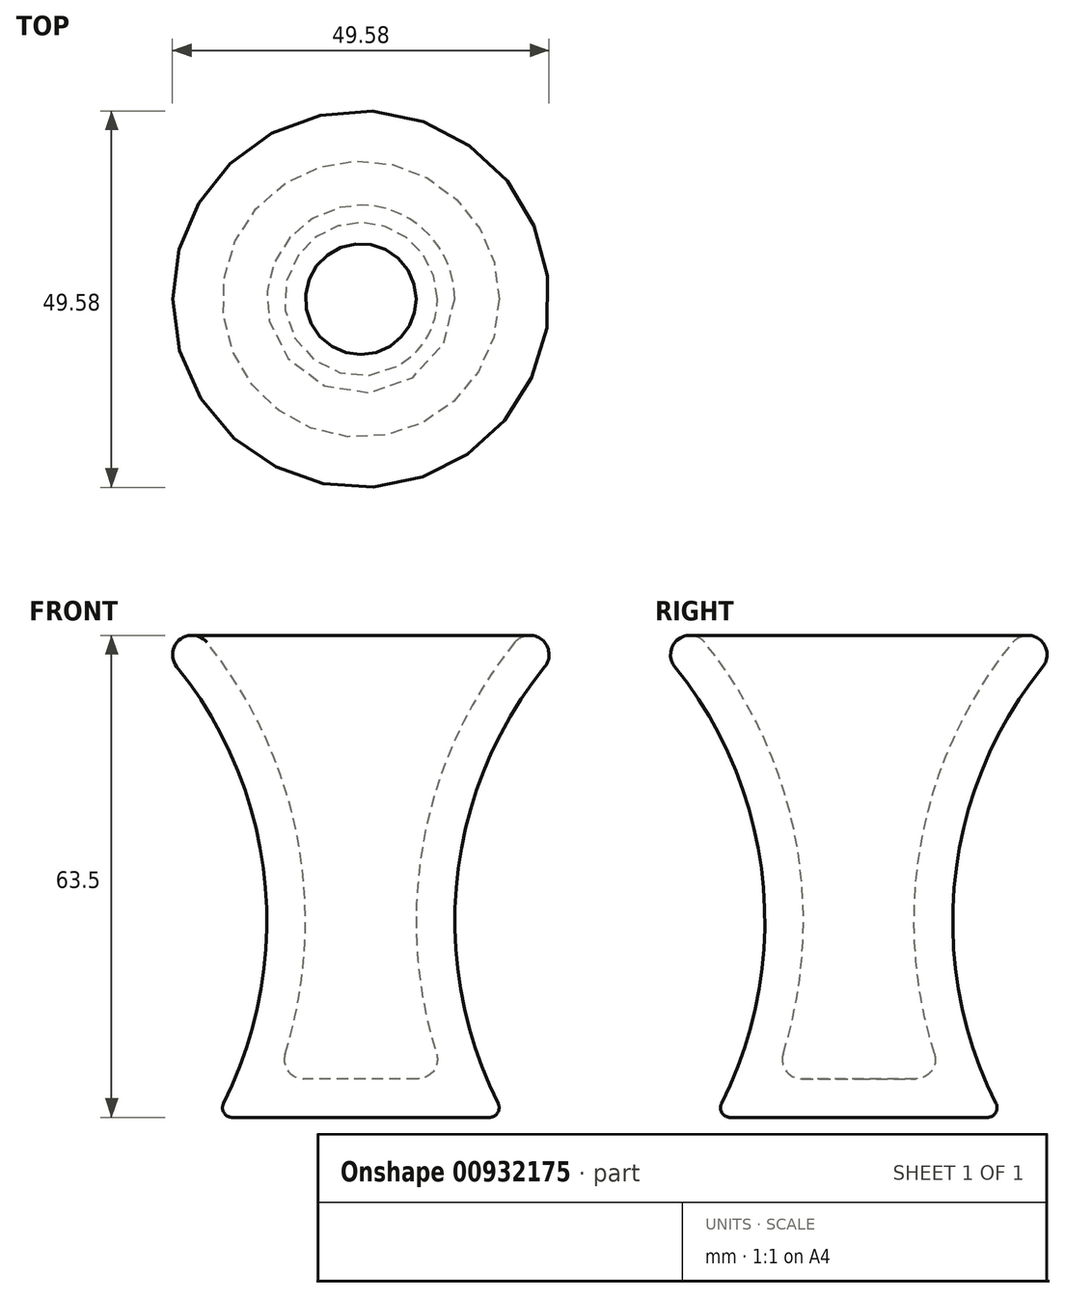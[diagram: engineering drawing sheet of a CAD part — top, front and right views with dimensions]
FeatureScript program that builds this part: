
annotation { "Feature Type Name" : "Feature", "Feature Type Description" : "" }
export const myFeature = defineFeature(function(context is Context, id is Id, definition is map)
    precondition{}
    {
        {
            var Q0;
            Q0=qCreatedBy(makeId("Front.planeOp"),FACE);
            var sketch = newSketch(context, id + "F0", { "sketchPlane" : qUnion([Q0])});
            skLineSegment(sketch, "E0", {"start": v(39.75, 49.1) * mm, "end": v(39.75, -14.4) * mm});
            skLineSegment(sketch, "E1", {"start": v(39.75, -14.4) * mm, "end": v(58.8, -14.4) * mm});
            skLineSegment(sketch, "E2", {"start": v(39.75, 49.1) * mm, "end": v(67.7, 49.1) * mm});
            skArc(sketch, "E3", {"start": v(67.7, 49.1) * mm, "mid": v(52.64, 18.84) * mm, "end": v(58.8, -14.4) * mm});
            skSolve(sketch);
        }
        {
            var Q0;
            Q0=makeQuery(id+"F0.imprint","IMPRINT",FACE,{"disambiguationData":[TD([[makeQuery(id+"F0.imprint","IMPRINT",EDGE,{"derivedFrom":sQuery(id+"F0.wireOp",EDGE,"E0")}),1.0]])]});
            var Q1;
            Q1=sQuery(id+"F0.wireOp",EDGE,"E0");
            revolve(context, id + "F1", {"surfaceOperationType" : NewSurfaceOperationType.NEW, "entities" : qUnion([Q0]), "axis" : qUnion([Q1]), "revolveType" : RevolveType.FULL});
        }
        {
            var Q0;
            Q0=makeQuery(id+"F1.opRevolve","SWEPT_FACE",FACE,{"disambiguationData":[OSD([sQuery(id+"F0.wireOp",EDGE,"E2")])]});
            shell(context, id + "F2", {"entities" : qUnion([Q0]), "thickness" : 5.08 * mm});
        }
        {
            var Q0;
            Q0=makeQuery(id+"F2.opShell","OFFSET_EDGE",EDGE,{"disambiguationData":[OSD([sQuery(id+"F0.wireOp",EDGE,"E2"),sQuery(id+"F0.wireOp",EDGE,"E3")])]});
            var Q1;
            Q1=makeQuery(id+"F1.opRevolve","SWEPT_EDGE",EDGE,{"disambiguationData":[OSD([sQuery(id+"F0.wireOp",EDGE,"E2"),sQuery(id+"F0.wireOp",EDGE,"E3")])]});
            fillet(context, id + "F3", {"entities" : qUnion([Q0, Q1]), "radius" : 2.54 * mm, "tangentPropagation" : true, "allowEdgeOverflow" : false});
        }
        {
            var Q0;
            Q0=makeQuery(id+"F2.opShell","OFFSET_EDGE",EDGE,{"disambiguationData":[OSD([sQuery(id+"F0.wireOp",EDGE,"E1"),sQuery(id+"F0.wireOp",EDGE,"E3")])]});
            fillet(context, id + "F4", {"entities" : qUnion([Q0]), "radius" : 2.54 * mm, "tangentPropagation" : true, "allowEdgeOverflow" : false});
        }
        {
            var Q0;
            Q0=makeQuery(id+"F1.opRevolve","SWEPT_EDGE",EDGE,{"disambiguationData":[OSD([sQuery(id+"F0.wireOp",EDGE,"E1"),sQuery(id+"F0.wireOp",EDGE,"E3")])]});
            fillet(context, id + "F5", {"entities" : qUnion([Q0]), "radius" : 1.27 * mm, "tangentPropagation" : true, "allowEdgeOverflow" : false});
        }
    });
